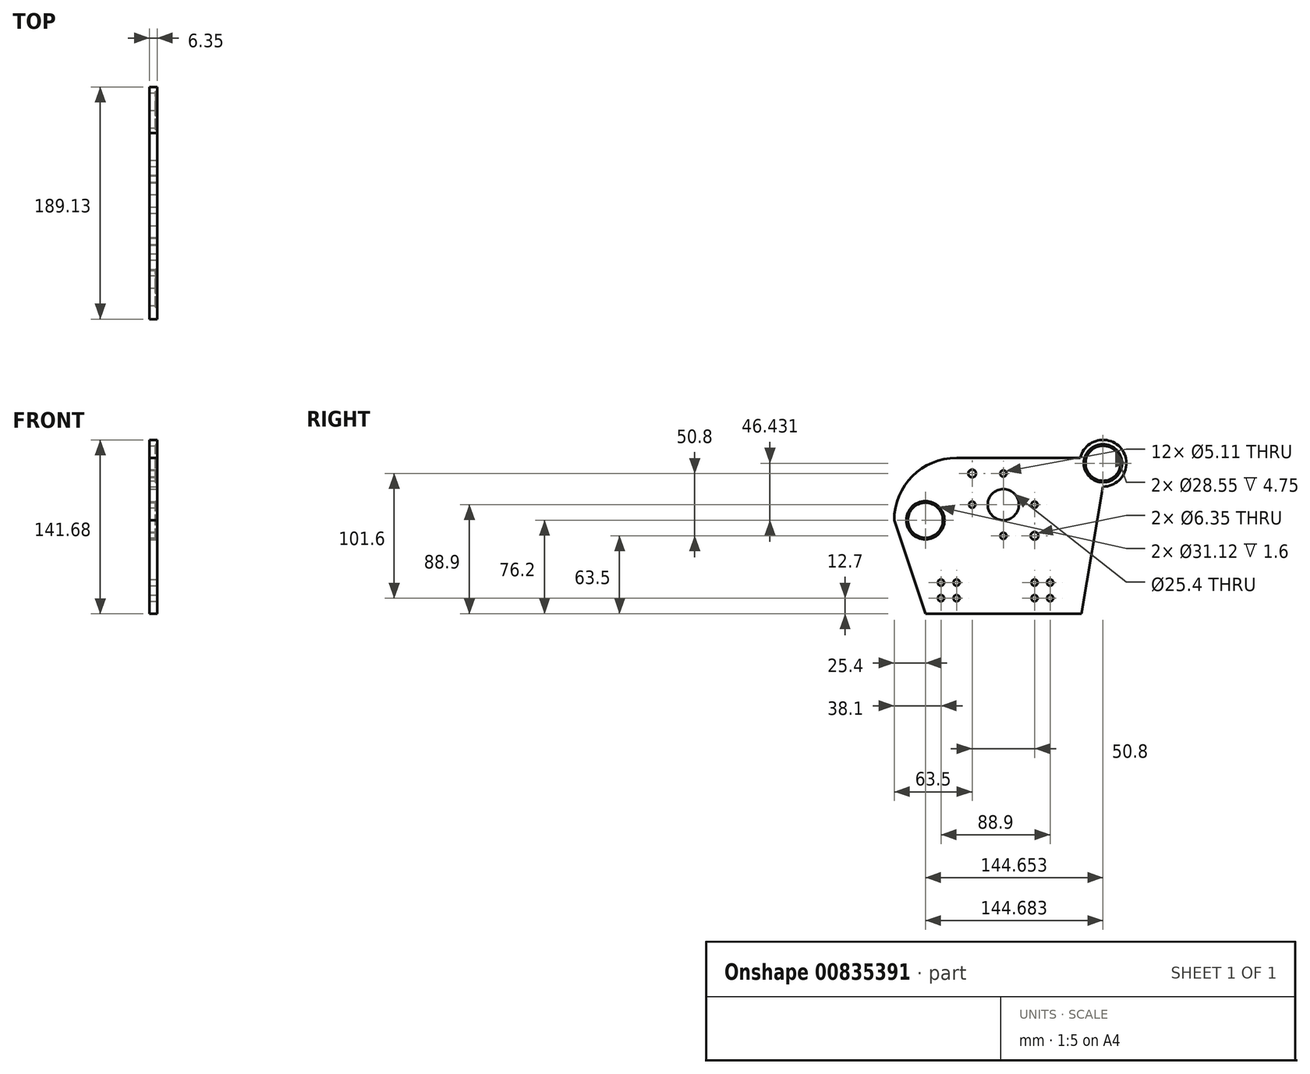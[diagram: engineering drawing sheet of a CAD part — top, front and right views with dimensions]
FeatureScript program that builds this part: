
annotation { "Feature Type Name" : "Feature", "Feature Type Description" : "" }
export const myFeature = defineFeature(function(context is Context, id is Id, definition is map)
    precondition{}
    {
        {
            var Q0;
            Q0=qCreatedBy(makeId("Right.planeOp"),FACE);
            var sketch = newSketch(context, id + "F0", { "sketchPlane" : qUnion([Q0])});
            skLineSegment(sketch, "E0.top", {"start": v(25.4, 127) * mm, "end": v(126.14, 127) * mm});
            skLineSegment(sketch, "E1", {"start": v(-25.4, 76.2) * mm, "end": v(0, 0) * mm});
            skArc(sketch, "E2", {"start": v(25.4, 127) * mm, "mid": v(-10.52, 112.12) * mm, "end": v(-25.4, 76.2) * mm});
            skPoint(sketch, "E3.end.orphan", {"position": v(144.68, 128.98) * mm});
            skPoint(sketch, "E4.end.orphan", {"position": v(141.66, 128.98) * mm});
            skPoint(sketch, "E5.end.orphan", {"position": v(136.5, 122.63) * mm});
            skPoint(sketch, "E6.start.orphan", {"position": v(147.67, 128.98) * mm});
            skPoint(sketch, "E7.start.orphan", {"position": v(152.9, 122.63) * mm});
            skPoint(sketch, "E8.orphan", {"position": v(147.67, 116.28) * mm});
            skPoint(sketch, "E9.0.midPoint", {"position": v(150.17, 125.8) * mm});
            skPoint(sketch, "E10.orphan", {"position": v(144.68, 122.63) * mm});
            skArc(sketch, "E11", {"start": v(144.68, 103.58) * mm, "mid": v(159.62, 134.46) * mm, "end": v(126.14, 127) * mm});
            skLineSegment(sketch, "E12", {"start": v(144.68, 103.58) * mm, "end": v(127, 0) * mm});
            skCircle(sketch, "E13", {"center": v(0, 76.2) * mm, "radius": 14.27 * mm});
            skCircle(sketch, "E14", {"center": v(38.1, 114.3) * mm, "radius": 3.18 * mm});
            skCircle(sketch, "E15", {"center": v(63.5, 88.9) * mm, "radius": 12.7 * mm});
            skCircle(sketch, "E16", {"center": v(63.5, 114.3) * mm, "radius": 2.55 * mm});
            skCircle(sketch, "E17", {"center": v(38.1, 88.9) * mm, "radius": 2.55 * mm});
            skCircle(sketch, "E18", {"center": v(88.9, 88.9) * mm, "radius": 2.55 * mm});
            skCircle(sketch, "E19", {"center": v(63.5, 63.5) * mm, "radius": 2.55 * mm});
            skCircle(sketch, "E20", {"center": v(88.9, 63.5) * mm, "radius": 3.18 * mm});
            skLineSegment(sketch, "E21.bottom", {"start": v(0, 0) * mm, "end": v(12.7, 0) * mm});
            skPoint(sketch, "E22.end.orphan", {"position": v(10.05, 0) * mm});
            skCircle(sketch, "E23", {"center": v(101.6, 25.4) * mm, "radius": 2.55 * mm});
            skCircle(sketch, "E24", {"center": v(101.6, 12.7) * mm, "radius": 2.55 * mm});
            skCircle(sketch, "E25", {"center": v(88.9, 25.4) * mm, "radius": 2.55 * mm});
            skCircle(sketch, "E26", {"center": v(88.9, 12.7) * mm, "radius": 2.55 * mm});
            skCircle(sketch, "E27", {"center": v(12.7, 25.4) * mm, "radius": 2.55 * mm});
            skCircle(sketch, "E28", {"center": v(12.7, 12.7) * mm, "radius": 2.55 * mm});
            skLineSegment(sketch, "E29.trimOffspring", {"start": v(12.7, 0) * mm, "end": v(25.4, 0) * mm});
            skCircle(sketch, "E30", {"center": v(25.4, 25.4) * mm, "radius": 2.55 * mm});
            skCircle(sketch, "E31", {"center": v(25.4, 12.7) * mm, "radius": 2.55 * mm});
            skPoint(sketch, "E32.orphan", {"position": v(25.4, 0) * mm});
            skLineSegment(sketch, "E33.trimOffspring", {"start": v(25.4, 0) * mm, "end": v(101.6, 0) * mm});
            skLineSegment(sketch, "E34.trimOffspring", {"start": v(101.6, 0) * mm, "end": v(127, 0) * mm});
            skPoint(sketch, "E35.center.orphan", {"position": v(38.1, 63.5) * mm});
            skPoint(sketch, "E36.center.orphan", {"position": v(88.9, 114.3) * mm});
            skPoint(sketch, "E37.orphan", {"position": v(148.32, 116.28) * mm});
            skPoint(sketch, "E9.0.end.orphan", {"position": v(151.99, 122.63) * mm});
            skPoint(sketch, "E38.trimOffspring.end.orphan", {"position": v(148.35, 128.98) * mm});
            skCircle(sketch, "E39", {"center": v(144.68, 122.63) * mm, "radius": 14.27 * mm});
            skSolve(sketch);
        }
        {
            var Q0;
            Q0 = qSketchRegion(id + "F0", true);
            extrude(context, id + "F1", {"entities" : qUnion([Q0]), "oppositeDirection" : true, "depth" : 6.35 * mm, "offsetDistance" : 25.4 * mm});
        }
        {
            var Q0;
            Q0=qCreatedBy(makeId("Right.planeOp"),FACE);
            var sketch = newSketch(context, id + "F2", { "sketchPlane" : qUnion([Q0])});
            skCircle(sketch, "E40", {"center": v(0, 76.2) * mm, "radius": 15.56 * mm});
            skCircle(sketch, "E41", {"center": v(144.65, 122.63) * mm, "radius": 15.56 * mm});
            skSolve(sketch);
        }
        {
            var Q0;
            Q0 = qSketchRegion(id + "F2", true);
            extrude(context, id + "F3", {"entities" : qUnion([Q0]), "operationType" : NewBodyOperationType.REMOVE, "oppositeDirection" : true, "depth" : 1.6 * mm, "offsetDistance" : 25.4 * mm});
        }
    });
